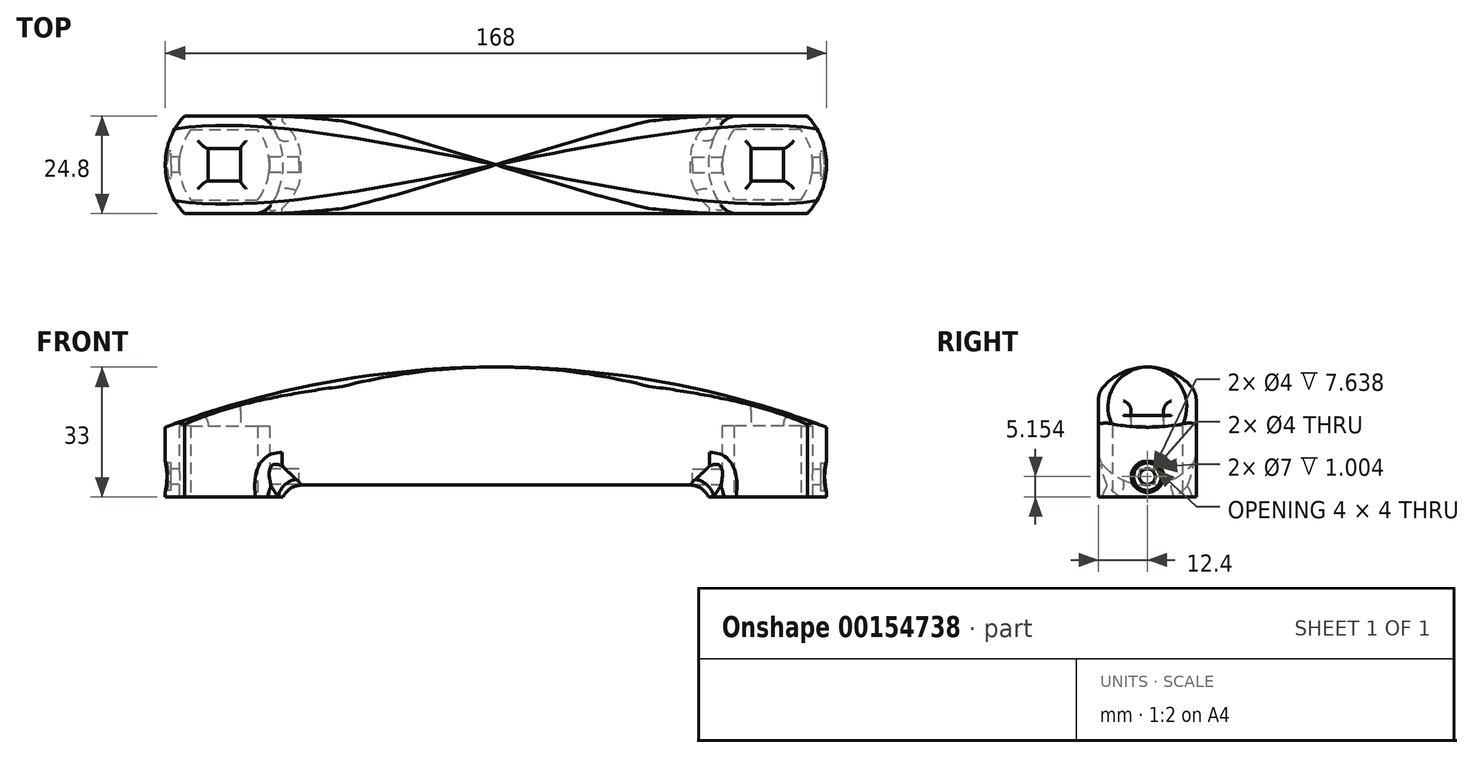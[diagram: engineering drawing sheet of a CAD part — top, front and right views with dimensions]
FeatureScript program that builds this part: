
annotation { "Feature Type Name" : "Feature", "Feature Type Description" : "" }
export const myFeature = defineFeature(function(context is Context, id is Id, definition is map)
    precondition{}
    {
        {
            var Q0;
            Q0=qCreatedBy(makeId("Top.planeOp"),FACE);
            var sketch = newSketch(context, id + "F0", { "sketchPlane" : qUnion([Q0])});
            skLineSegment(sketch, "E0.bottom", {"start": v(-80.5, 8.9) * mm, "end": v(-77.5, 8.9) * mm, "construction": true});
            skLineSegment(sketch, "E0.top", {"start": v(-80.5, -8.9) * mm, "end": v(-77.5, -8.9) * mm, "construction": true});
            skLineSegment(sketch, "E0.left", {"start": v(-80.5, 8.9) * mm, "end": v(-80.5, -8.9) * mm, "construction": true});
            skLineSegment(sketch, "E0.right", {"start": v(-57.5, 8.9) * mm, "end": v(-57.5, -8.9) * mm, "construction": true});
            skArc(sketch, "E1", {"start": v(-77.5, 8.9) * mm, "mid": v(-80.5, 0) * mm, "end": v(-77.5, -8.9) * mm});
            skLineSegment(sketch, "E2", {"start": v(-69, 8.9) * mm, "end": v(-69, -8.9) * mm, "construction": true});
            skArc(sketch, "E3.MirrorCS", {"start": v(-60.5, 8.9) * mm, "mid": v(-57.5, 0) * mm, "end": v(-60.5, -8.9) * mm});
            skLineSegment(sketch, "E4", {"start": v(-80.5, 0) * mm, "end": v(-57.5, 0) * mm, "construction": true});
            skPoint(sketch, "E4.startSnap0", {"position": v(-80.5, 0) * mm});
            skLineSegment(sketch, "E5", {"start": v(-77.5, 8.9) * mm, "end": v(-77.5, -8.9) * mm, "construction": true});
            skLineSegment(sketch, "E6", {"start": v(0, 8.37) * mm, "end": v(0, -11.71) * mm, "construction": true});
            skLineSegment(sketch, "E7", {"start": v(-77.5, 8.9) * mm, "end": v(-60.5, 8.9) * mm});
            skLineSegment(sketch, "E8", {"start": v(-60.5, 8.9) * mm, "end": v(-57.5, 8.9) * mm, "construction": true});
            skLineSegment(sketch, "E9", {"start": v(-60.5, -8.9) * mm, "end": v(-60.5, -8.9) * mm});
            skLineSegment(sketch, "E10", {"start": v(-77.5, -8.9) * mm, "end": v(-60.5, -8.9) * mm});
            skLineSegment(sketch, "E11", {"start": v(-60.5, -8.9) * mm, "end": v(-57.5, -8.9) * mm, "construction": true});
            skCircle(sketch, "E12", {"center": v(0, 0) * mm, "radius": 85 * mm, "construction": true});
            skSolve(sketch);
        }
        {
            var Q0;
            Q0=qCreatedBy(makeId("Top.planeOp"),FACE);
            var sketch = newSketch(context, id + "F1", { "sketchPlane" : qUnion([Q0])});
            skLineSegment(sketch, "E13.0", {"start": v(-79.12, 12.4) * mm, "end": v(-58.88, 12.4) * mm});
            skArc(sketch, "E13.1", {"start": v(-79.12, 12.4) * mm, "mid": v(-84, 0) * mm, "end": v(-79.12, -12.4) * mm});
            skLineSegment(sketch, "E13.2", {"start": v(-79.12, -12.4) * mm, "end": v(-58.88, -12.4) * mm});
            skArc(sketch, "E13.3", {"start": v(-58.88, 12.4) * mm, "mid": v(-54, 0) * mm, "end": v(-58.88, -12.4) * mm});
            skCircle(sketch, "E14", {"center": v(0, 0) * mm, "radius": 85 * mm, "construction": true});
            skSolve(sketch);
        }
        {
            var Q0;
            Q0=qCreatedBy(makeId("Front.planeOp"),FACE);
            var sketch = newSketch(context, id + "F2", { "sketchPlane" : qUnion([Q0])});
            skLineSegment(sketch, "E15", {"start": v(0, 18) * mm, "end": v(-39.65, 18) * mm, "construction": true});
            skPoint(sketch, "E16.oppositeSnap0", {"position": v(-19.82, 18) * mm});
            skLineSegment(sketch, "E16.bottom", {"start": v(0, 3) * mm, "end": v(-95, 3) * mm});
            skLineSegment(sketch, "E16.top", {"start": v(0, 18) * mm, "end": v(-95, 18) * mm});
            skLineSegment(sketch, "E16.left", {"start": v(0, 3) * mm, "end": v(0, 18) * mm});
            skLineSegment(sketch, "E16.right", {"start": v(-95, 3) * mm, "end": v(-95, 18) * mm});
            skSolve(sketch);
        }
        {
            var Q0;
            Q0 = qSketchRegion(id + "F2", true);
            var Q1;
            Q1=sQuery(id+"F2.wireOp",EDGE,"E16.top");
            revolve(context, id + "F3", {"entities" : qUnion([Q0]), "axis" : qUnion([Q1]), "revolveType" : RevolveType.FULL});
        }
        {
            var Q0;
            Q0=qCreatedBy(makeId("Top.planeOp"),FACE);
            var sketch = newSketch(context, id + "F4", { "sketchPlane" : qUnion([Q0])});
            skArc(sketch, "E17", {"start": v(-79.12, 12.4) * mm, "mid": v(-84, 0) * mm, "end": v(-79.12, -12.4) * mm});
            skLineSegment(sketch, "E18", {"start": v(-79.12, 12.4) * mm, "end": v(0, 12.4) * mm});
            skLineSegment(sketch, "E19", {"start": v(0, 12.4) * mm, "end": v(0, 20.08) * mm});
            skLineSegment(sketch, "E20", {"start": v(0, 20.08) * mm, "end": v(-96.67, 20.08) * mm});
            skLineSegment(sketch, "E21", {"start": v(-96.67, 20.08) * mm, "end": v(-96.67, -24.17) * mm});
            skLineSegment(sketch, "E22", {"start": v(-96.67, -24.17) * mm, "end": v(0, -24.17) * mm});
            skLineSegment(sketch, "E23", {"start": v(0, -24.17) * mm, "end": v(0, -12.4) * mm});
            skLineSegment(sketch, "E24", {"start": v(0, -12.4) * mm, "end": v(-79.12, -12.4) * mm});
            skSolve(sketch);
        }
        {
            var Q0;
            Q0 = qSketchRegion(id + "F4", true);
            extrude(context, id + "F5", {"entities" : qUnion([Q0]), "operationType" : NewBodyOperationType.REMOVE, "depth" : 50 * mm});
        }
        {
            var Q0;
            Q0=qSketchRegion(id+"F1",true);
            extrude(context, id + "F6", {"entities" : qUnion([Q0]), "operationType" : NewBodyOperationType.ADD, "depth" : 23 * mm});
        }
        {
            var Q0;
            Q0=qSketchRegion(id+"F0",true);
            extrude(context, id + "F7", {"entities" : qUnion([Q0]), "operationType" : NewBodyOperationType.REMOVE, "depth" : 18 * mm});
        }
        {
            var Q0;
            Q0=makeQuery(id+"F7.boolean.opBoolean","COPY",FACE,{"derivedFrom":makeQuery(id+"F7.opExtrude","CAP_FACE",FACE,{"disambiguationData":[OSD([sQuery(id+"F0.wireOp",EDGE,"E1"),sQuery(id+"F0.wireOp",EDGE,"E3.MirrorCS"),sQuery(id+"F0.wireOp",EDGE,"E7"),sQuery(id+"F0.wireOp",EDGE,"E10")])],"isStart":false})});
            var sketch = newSketch(context, id + "F8", { "sketchPlane" : qUnion([Q0])});
            skLineSegment(sketch, "E25.bottom", {"start": v(-73.13, 4.12) * mm, "end": v(-64.87, 4.12) * mm});
            skLineSegment(sketch, "E25.top", {"start": v(-73.13, -4.12) * mm, "end": v(-64.87, -4.12) * mm});
            skLineSegment(sketch, "E25.left", {"start": v(-73.13, 4.12) * mm, "end": v(-73.13, -4.12) * mm});
            skLineSegment(sketch, "E25.right", {"start": v(-64.88, 4.13) * mm, "end": v(-64.88, -4.13) * mm});
            skLineSegment(sketch, "E26", {"start": v(-69, 4.12) * mm, "end": v(-69, -4.12) * mm, "construction": true});
            skLineSegment(sketch, "E27", {"start": v(-73.13, 0) * mm, "end": v(-64.88, 0) * mm, "construction": true});
            skSolve(sketch);
        }
        {
            var Q0;
            Q0=qSketchRegion(id+"F8",true);
            var Q1;
            Q1=makeQuery(id+"F6.opExtrude","CAP_FACE",FACE,{"disambiguationData":[OSD([sQuery(id+"F1.wireOp",EDGE,"E13.0"),sQuery(id+"F1.wireOp",EDGE,"E13.1"),sQuery(id+"F1.wireOp",EDGE,"E13.2"),sQuery(id+"F1.wireOp",EDGE,"E13.3")])],"isStart":false});
            extrude(context, id + "F9", {"entities" : qUnion([Q0]), "operationType" : NewBodyOperationType.REMOVE, "endBound" : BoundingType.THROUGH_ALL, "oppositeDirection" : true, "endBoundEntityFace" : qUnion([Q1]), "depth" : 25 * mm});
        }
        {
            var Q0;
            Q0=qCreatedBy(makeId("Right.planeOp"),FACE);
            cPlane(context, id + "F10", {"entities" : qUnion([Q0]), "cplaneType" : CPlaneType.OFFSET, "offset" : 90 * mm, "oppositeDirection" : true, "width" : 150 * mm, "height" : 150 * mm});
        }
        {
            var Q0;
            Q0=qCreatedBy(id+"F10.planeOp",FACE);
            var sketch = newSketch(context, id + "F11", { "sketchPlane" : qUnion([Q0])});
            skCircle(sketch, "E28", {"center": v(0, 5.15) * mm, "radius": 2 * mm});
            skSolve(sketch);
        }
        {
            var Q0;
            Q0 = qSketchRegion(id + "F11", true);
            extrude(context, id + "F12", {"entities" : qUnion([Q0]), "operationType" : NewBodyOperationType.REMOVE, "flatOperationType" : FlatOperationType.REMOVE, "offsetDistance" : 25 * mm, "depth" : 40 * mm, "domain" : OperationDomain.MODEL});
        }
        {
            var Q0;
            Q0=qCreatedBy(id+"F10.planeOp",FACE);
            var sketch = newSketch(context, id + "F13", { "sketchPlane" : qUnion([Q0])});
            skCircle(sketch, "E29", {"center": v(0, 5.15) * mm, "radius": 3.5 * mm});
            skSolve(sketch);
        }
        {
            var Q0;
            Q0 = qSketchRegion(id + "F13", true);
            extrude(context, id + "F14", {"entities" : qUnion([Q0]), "operationType" : NewBodyOperationType.REMOVE, "depth" : 7.5 * mm});
        }
        {
            var Q0;
            Q0=qCreatedBy(makeId("Front.planeOp"),FACE);
            var sketch = newSketch(context, id + "F15", { "sketchPlane" : qUnion([Q0])});
            skLineSegment(sketch, "E30", {"start": v(-64.87, 24) * mm, "end": v(-80.29, 24) * mm, "construction": true});
            skLineSegment(sketch, "E31", {"start": v(-64.87, 18) * mm, "end": v(-80.42, 18) * mm, "construction": true});
            skLineSegment(sketch, "E32", {"start": v(-64.87, 24) * mm, "end": v(-64.87, 18) * mm, "construction": true});
            skSolve(sketch);
        }
        {
            var Q0;
            Q0=qCreatedBy(makeId("Front.planeOp"),FACE);
            var sketch = newSketch(context, id + "F16", { "sketchPlane" : qUnion([Q0])});
            skArc(sketch, "E33", {"start": v(-110.68, 5.74) * mm, "mid": v(-57, 26.08) * mm, "end": v(0, 33) * mm});
            skLineSegment(sketch, "E34", {"start": v(0, 33) * mm, "end": v(-86, 33) * mm, "construction": true});
            skLineSegment(sketch, "E35", {"start": v(-86, 33) * mm, "end": v(-86, 0) * mm, "construction": true});
            skLineSegment(sketch, "E36", {"start": v(-110.68, 5.74) * mm, "end": v(-110.32, 10.3) * mm});
            skLineSegment(sketch, "E37", {"start": v(-110.32, 10.3) * mm, "end": v(-110.32, 55.99) * mm});
            skLineSegment(sketch, "E38", {"start": v(-110.32, 55.99) * mm, "end": v(0, 55.99) * mm});
            skLineSegment(sketch, "E39", {"start": v(0, 55.99) * mm, "end": v(0, 33) * mm});
            skPoint(sketch, "E40", {"position": v(-86, 16.5) * mm});
            skLineSegment(sketch, "E41", {"start": v(-79.12, 18) * mm, "end": v(-79.15, 19.47) * mm, "construction": true});
            skSolve(sketch);
        }
        {
            var Q0;
            Q0 = qSketchRegion(id + "F16", true);
            extrude(context, id + "F17", {"entities" : qUnion([Q0]), "operationType" : NewBodyOperationType.REMOVE, "oppositeDirection" : true, "depth" : 50 * mm, "symmetric" : true});
        }
        {
            var Q0;
            Q0=makeQuery(id+"F17.boolean.opBoolean","INTERSECT",EDGE,{"disambiguationData":[OD(1.0)],"derivedFrom":[makeQuery(id+"F5.boolean.opBoolean","SPLIT",FACE,{"disambiguationData":[OD(1.0)],"derivedFrom":makeQuery(id+"F3.opRevolve","SWEPT_FACE",FACE,{"disambiguationData":[OSD([sQuery(id+"F2.wireOp",EDGE,"E16.bottom")])]})}),makeQuery(id+"F17.opExtrude","SWEPT_FACE",FACE,{"disambiguationData":[OSD([sQuery(id+"F16.wireOp",EDGE,"E33")])]})]});
            var Q1;
            Q1=makeQuery(id+"F5.boolean.opBoolean","INTERSECT",EDGE,{"disambiguationData":[OD(1.0)],"derivedFrom":[makeQuery(id+"F3.opRevolve","SWEPT_FACE",FACE,{"disambiguationData":[OSD([sQuery(id+"F2.wireOp",EDGE,"E16.bottom")])]}),makeQuery(id+"F5.opExtrude","SWEPT_FACE",FACE,{"disambiguationData":[OSD([sQuery(id+"F4.wireOp",EDGE,"E24")])]})]});
            var Q2;
            Q2=makeQuery(id+"F17.boolean.opBoolean","INTERSECT",EDGE,{"disambiguationData":[OD(0.0)],"derivedFrom":[makeQuery(id+"F5.boolean.opBoolean","SPLIT",FACE,{"disambiguationData":[OD(1.0)],"derivedFrom":makeQuery(id+"F3.opRevolve","SWEPT_FACE",FACE,{"disambiguationData":[OSD([sQuery(id+"F2.wireOp",EDGE,"E16.bottom")])]})}),makeQuery(id+"F17.opExtrude","SWEPT_FACE",FACE,{"disambiguationData":[OSD([sQuery(id+"F16.wireOp",EDGE,"E33")])]})]});
            var Q3;
            Q3=makeQuery(id+"F5.boolean.opBoolean","INTERSECT",EDGE,{"disambiguationData":[OD(1.0)],"derivedFrom":[makeQuery(id+"F3.opRevolve","SWEPT_FACE",FACE,{"disambiguationData":[OSD([sQuery(id+"F2.wireOp",EDGE,"E16.bottom")])]}),makeQuery(id+"F5.opExtrude","SWEPT_FACE",FACE,{"disambiguationData":[OSD([sQuery(id+"F4.wireOp",EDGE,"E18")])]})]});
            var Q4;
            Q4=makeQuery(id+"F6.boolean.opBoolean","INTERSECT",EDGE,{"derivedFrom":[makeQuery(id+"F5.boolean.opBoolean","SPLIT",FACE,{"disambiguationData":[OD(0.0)],"derivedFrom":makeQuery(id+"F3.opRevolve","SWEPT_FACE",FACE,{"disambiguationData":[OSD([sQuery(id+"F2.wireOp",EDGE,"E16.bottom")])]})}),makeQuery(id+"F6.opExtrude","SWEPT_FACE",FACE,{"disambiguationData":[OSD([sQuery(id+"F1.wireOp",EDGE,"E13.3")])]})]});
            var Q5;
            Q5=makeQuery(id+"F5.boolean.opBoolean","INTERSECT",EDGE,{"disambiguationData":[OD(0.0)],"derivedFrom":[makeQuery(id+"F3.opRevolve","SWEPT_FACE",FACE,{"disambiguationData":[OSD([sQuery(id+"F2.wireOp",EDGE,"E16.bottom")])]}),makeQuery(id+"F5.opExtrude","SWEPT_FACE",FACE,{"disambiguationData":[OSD([sQuery(id+"F4.wireOp",EDGE,"E18")])]})]});
            var Q6;
            Q6=makeQuery(id+"F5.boolean.opBoolean","INTERSECT",EDGE,{"disambiguationData":[OD(0.0)],"derivedFrom":[makeQuery(id+"F3.opRevolve","SWEPT_FACE",FACE,{"disambiguationData":[OSD([sQuery(id+"F2.wireOp",EDGE,"E16.bottom")])]}),makeQuery(id+"F5.opExtrude","SWEPT_FACE",FACE,{"disambiguationData":[OSD([sQuery(id+"F4.wireOp",EDGE,"E24")])]})]});
            fillet(context, id + "F18", {"entities" : qUnion([Q0, Q1, Q2, Q3, Q4, Q5, Q6]), "radius" : 5 * mm, "tangentPropagation" : true, "allowEdgeOverflow" : false});
        }
        {
            var Q0;
            Q0=makeQuery(id+"F17.boolean.opBoolean","INTERSECT",EDGE,{"derivedFrom":[makeQuery(id+"F9.boolean.opBoolean","COPY",FACE,{"derivedFrom":makeQuery(id+"F9.opExtrude","SWEPT_FACE",FACE,{"disambiguationData":[OSD([sQuery(id+"F8.wireOp",EDGE,"E25.top")])]})}),makeQuery(id+"F17.opExtrude","SWEPT_FACE",FACE,{"disambiguationData":[OSD([sQuery(id+"F16.wireOp",EDGE,"E33")])]})]});
            var Q1;
            Q1=makeQuery(id+"F17.boolean.opBoolean","INTERSECT",EDGE,{"derivedFrom":[makeQuery(id+"F9.boolean.opBoolean","COPY",FACE,{"derivedFrom":makeQuery(id+"F9.opExtrude","SWEPT_FACE",FACE,{"disambiguationData":[OSD([sQuery(id+"F8.wireOp",EDGE,"E25.right")])]})}),makeQuery(id+"F17.opExtrude","SWEPT_FACE",FACE,{"disambiguationData":[OSD([sQuery(id+"F16.wireOp",EDGE,"E33")])]})]});
            var Q2;
            Q2=makeQuery(id+"F17.boolean.opBoolean","INTERSECT",EDGE,{"derivedFrom":[makeQuery(id+"F9.boolean.opBoolean","COPY",FACE,{"derivedFrom":makeQuery(id+"F9.opExtrude","SWEPT_FACE",FACE,{"disambiguationData":[OSD([sQuery(id+"F8.wireOp",EDGE,"E25.left")])]})}),makeQuery(id+"F17.opExtrude","SWEPT_FACE",FACE,{"disambiguationData":[OSD([sQuery(id+"F16.wireOp",EDGE,"E33")])]})]});
            var Q3;
            Q3=makeQuery(id+"F17.boolean.opBoolean","INTERSECT",EDGE,{"derivedFrom":[makeQuery(id+"F9.boolean.opBoolean","COPY",FACE,{"derivedFrom":makeQuery(id+"F9.opExtrude","SWEPT_FACE",FACE,{"disambiguationData":[OSD([sQuery(id+"F8.wireOp",EDGE,"E25.bottom")])]})}),makeQuery(id+"F17.opExtrude","SWEPT_FACE",FACE,{"disambiguationData":[OSD([sQuery(id+"F16.wireOp",EDGE,"E33")])]})]});
            fillet(context, id + "F19", {"entities" : qUnion([Q0, Q1, Q2, Q3]), "radius" : 2 * mm, "tangentPropagation" : true, "allowEdgeOverflow" : false});
        }
        {
            var Q0;
            Q0=makeQuery(id+"F14.boolean.opBoolean","INTERSECT",EDGE,{"derivedFrom":[makeQuery(id+"F6.boolean.opBoolean","MERGE",FACE,{"derivedFrom":[makeQuery(id+"F5.boolean.opBoolean","COPY",FACE,{"derivedFrom":makeQuery(id+"F5.opExtrude","SWEPT_FACE",FACE,{"disambiguationData":[OSD([sQuery(id+"F4.wireOp",EDGE,"E17")])]})}),makeQuery(id+"F6.opExtrude","SWEPT_FACE",FACE,{"disambiguationData":[OSD([sQuery(id+"F1.wireOp",EDGE,"E13.1")])]})]}),makeQuery(id+"F14.opExtrude","SWEPT_FACE",FACE,{"disambiguationData":[OSD([sQuery(id+"F13.wireOp",EDGE,"E29")])]})]});
            fillet(context, id + "F20", {"entities" : qUnion([Q0]), "radius" : 0.5 * mm, "tangentPropagation" : true, "allowEdgeOverflow" : false});
        }
        {
            var Q0;
            Q0=makeQuery(id+"F3.opRevolve","SWEPT_BODY",BODY,{"disambiguationData":[OSD([sQuery(id+"F2.wireOp",EDGE,"E16.bottom"),sQuery(id+"F2.wireOp",EDGE,"E16.top"),sQuery(id+"F2.wireOp",EDGE,"E16.left"),sQuery(id+"F2.wireOp",EDGE,"E16.right")])]});
            var Q1;
            Q1=makeQuery(id+"F3.opRevolve","SWEPT_FACE",FACE,{"disambiguationData":[OSD([sQuery(id+"F2.wireOp",EDGE,"E16.left")])]});
            mirror(context, id + "F21", {"operationType" : NewBodyOperationType.ADD, "entities" : qUnion([Q0]), "mirrorPlane" : qUnion([Q1])});
        }
    });
